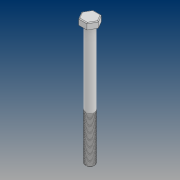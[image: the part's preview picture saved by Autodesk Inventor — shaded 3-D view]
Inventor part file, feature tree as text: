
AUTODESK INVENTOR PART (.ipt)
format: ipt  version: 2021 (Build 250183000, 183)  size: 547,840 bytes
history: native  units: mm
features: sketch x3, extrude x1, revolve x1, chamfer x1, helix x1, fillet x1, projected_geometry x1
ambient origin geometry x8: Origin, YZ Plane, XZ Plane, XY Plane, X Axis, Y Axis, Z Axis, Center Point
bodies: Solid1 (feature_tree)
feature tree (9):
  extrude  "Extrusion1"  Depth=4.0mm TaperAngle=0.0deg
  revolve  "Revolution1"  [1 undecoded]
  chamfer  "Chamfer1"  Distance=0.5mm Angle=45.0deg
  helix  "Coil1"  [1 undecoded]
  fillet  "Fillet1"  Radius=0.5mm
  sketch  "Sketch1"  dims[d0=9.5mm d1=4.0mm d2=0.0mm]
  sketch  "Sketch2"  dims[d3=3.0mm d4=80.0mm]
  sketch  "Sketch3"  dims[d5=90.0deg d6=0.5mm d7=2.0mm d8=45.0deg d9=60.0deg d10=0.5mm d11=0.5mm d12=30.0mm d13=10.0mm d14=0.0mm d15=90.0deg d16=90.0deg d17=0.0mm d18=0.0mm d19=0.5mm]
  projected_geometry  "Projected Loop1"
note: 2 required parameter values undecoded (feature->parameter linkage not recoverable at this tier; creation-order binding heuristic only, values carry confidence <= 0.55)